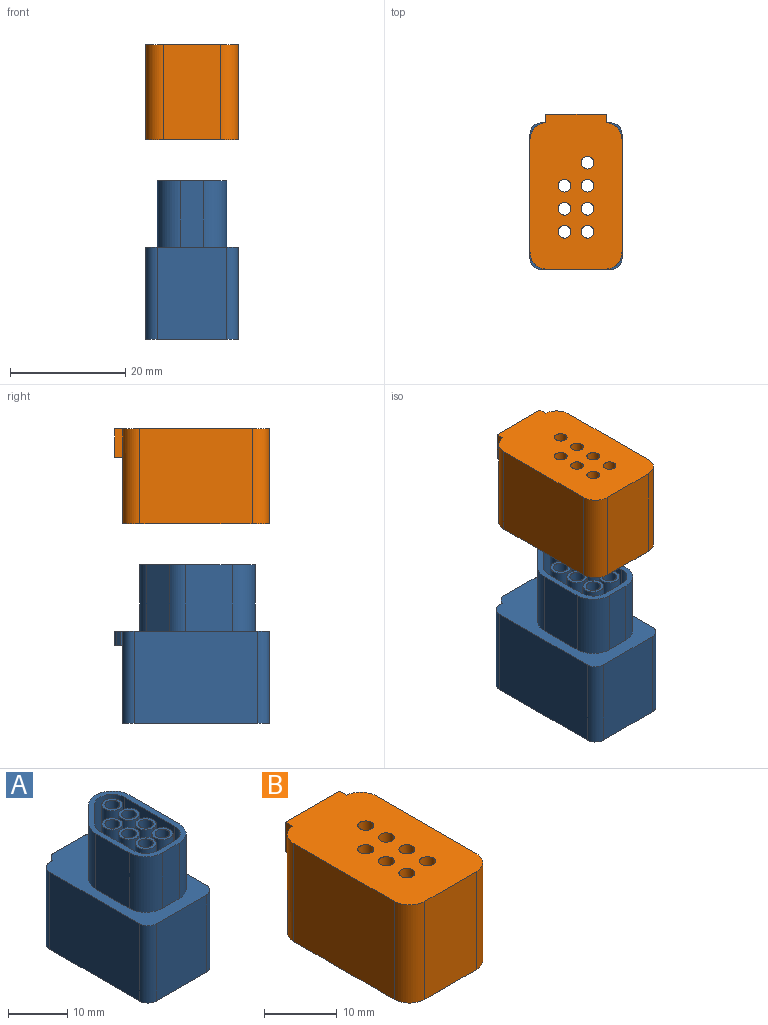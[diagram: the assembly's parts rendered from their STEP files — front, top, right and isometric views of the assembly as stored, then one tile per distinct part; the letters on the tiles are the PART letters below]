
ASSEMBLY  parts=2 mates=1
PART A: 66 faces, bbox 16x26.9x27.5 mm
  f0: cylinder r=1.25mm len=14.7mm, axis (0,0,1), area 115.5mm2, adj f17,f65
  f1: cylinder r=1.25mm len=14.7mm, axis (0,0,1), area 115.5mm2, adj f19,f65
  f2: cylinder r=1.25mm len=14.7mm, axis (0,0,1), area 115.5mm2, adj f21,f65
  f3: cylinder r=1.25mm len=14.7mm, axis (0,0,1), area 115.5mm2, adj f23,f65
  f4: cylinder r=1.25mm len=14.7mm, axis (0,0,1), area 115.5mm2, adj f25,f65
  f5: cylinder r=1.25mm len=14.7mm, axis (0,0,1), area 115.5mm2, adj f27,f65
  f6: cylinder r=1.25mm len=14.7mm, axis (0,0,1), area 115.5mm2, adj f15,f65
  f7: plane 18x10mm, normal (0,0,1), area 86mm2, adj f14,f16,f18,f20,f22,f24,f26,f35
  f8: plane 16x12mm, normal (0,1,0), area 165.7mm2, adj f12,f13,f45,f48,f49,f51,f52
  f9: plane 21.5x16mm, normal (-1,0,0), area 344mm2, adj f12,f13,f45,f46
  f10: plane 16x12mm, normal (0,-1,0), area 192mm2, adj f12,f13,f46,f47
  f11: plane 21.5x16mm, normal (1,0,0), area 344mm2, adj f12,f13,f47,f48
  f12: plane 25.5x16mm, normal (0,0,-1), area 150mm2, adj f8,f9,f10,f11,f45,f46,f47,f48
  f13: plane 26.9x16mm, normal (0,0,1), area 209.3mm2, adj f8,f9,f10,f11,f28,f29,f30,f31
  f14: cylinder r=1.8mm len=11.5mm, axis (0,0,-1), area 130.1mm2, adj f7,f15
  f15: plane 3.6x3.6mm, normal (0,0,1), area 5.3mm2, adj f6,f14
  f16: cylinder r=1.8mm len=11.5mm, axis (0,0,-1), area 130.1mm2, adj f7,f17
  f17: plane 3.6x3.6mm, normal (0,0,1), area 5.3mm2, adj f0,f16
  f18: cylinder r=1.8mm len=11.5mm, axis (0,0,-1), area 130.1mm2, adj f7,f19
  f19: plane 3.6x3.6mm, normal (0,0,1), area 5.3mm2, adj f1,f18
  f20: cylinder r=1.8mm len=11.5mm, axis (0,0,-1), area 130.1mm2, adj f7,f21
  f21: plane 3.6x3.6mm, normal (0,0,1), area 5.3mm2, adj f2,f20
  f22: cylinder r=1.8mm len=11.5mm, axis (0,0,-1), area 130.1mm2, adj f7,f23
  f23: plane 3.6x3.6mm, normal (0,0,1), area 5.3mm2, adj f3,f22
  f24: cylinder r=1.8mm len=11.5mm, axis (0,0,-1), area 130.1mm2, adj f7,f25
  f25: plane 3.6x3.6mm, normal (0,0,1), area 5.3mm2, adj f4,f24
  f26: cylinder r=1.8mm len=11.5mm, axis (0,0,-1), area 130.1mm2, adj f7,f27
  f27: plane 3.6x3.6mm, normal (0,0,1), area 5.3mm2, adj f5,f26
  f28: cylinder r=4mm len=11.5mm, axis (0,0,-1), area 72.3mm2, adj f13,f29,f43,f44
  f29: plane 11.5x4mm, normal (0,-1,0), area 46mm2, adj f13,f28,f30,f44
  f30: cylinder r=4mm len=11.5mm, axis (0,0,-1), area 72.3mm2, adj f13,f29,f31,f44
  f31: plane 12x11.5mm, normal (1,0,0), area 138mm2, adj f13,f30,f32,f44
  f32: cylinder r=4mm len=11.5mm, axis (0,0,-1), area 108.4mm2, adj f13,f31,f33,f44
  f33: plane 11.5x4mm, normal (-0.71,0.71,0), area 65.1mm2, adj f13,f32,f34,f44
  f34: cylinder r=4mm len=11.5mm, axis (0,0,-1), area 36.1mm2, adj f13,f33,f43,f44
  f35: cylinder r=3mm len=11.5mm, axis (0,0,-1), area 81.3mm2, adj f7,f36,f42,f44
  f36: plane 12x11.5mm, normal (-1,0,0), area 138mm2, adj f7,f35,f37,f44
  f37: cylinder r=3mm len=11.5mm, axis (0,0,-1), area 54.2mm2, adj f7,f36,f38,f44
  f38: plane 11.5x4mm, normal (0,1,0), area 46mm2, adj f7,f37,f39,f44
  f39: cylinder r=3mm len=11.5mm, axis (0,0,-1), area 54.2mm2, adj f7,f38,f40,f44
  f40: plane 11.5x8mm, normal (1,0,0), area 92mm2, adj f7,f39,f41,f44
  f41: cylinder r=3mm len=11.5mm, axis (0,0,-1), area 27.1mm2, adj f7,f40,f42,f44
  f42: plane 11.5x4mm, normal (0.71,-0.71,0), area 65.1mm2, adj f7,f35,f41,f44
  f43: plane 11.5x8mm, normal (-1,0,0), area 92mm2, adj f13,f28,f34,f44
  f44: plane 20x12mm, normal (0,0,1), area 51.6mm2, adj f28,f29,f30,f31,f32,f33,f34,f35
  f45: cylinder r=2mm len=16mm, axis (0,0,-1), area 50.3mm2, adj f8,f9,f12,f13
  f46: cylinder r=2mm len=16mm, axis (0,0,1), area 50.3mm2, adj f9,f10,f12,f13
  f47: cylinder r=2mm len=16mm, axis (0,0,-1), area 50.3mm2, adj f10,f11,f12,f13
  f48: cylinder r=2mm len=16mm, axis (0,0,1), area 50.3mm2, adj f8,f11,f12,f13
  f49: plane 2.5x0.4mm, normal (1,0,0), area 1mm2, adj f8,f13,f52,f54
  f50: plane 7.67x2.5mm, normal (0,1,0), area 19.2mm2, adj f13,f52,f55,f56
  f51: plane 2.5x0.4mm, normal (-1,0,0), area 1mm2, adj f8,f13,f52,f53
  f52: plane 10.5x1.4mm, normal (0,0,-1), area 13.7mm2, adj f8,f49,f50,f51,f53,f54,f55,f56
  f53: plane 2.5x0.71mm, normal (-0.71,0.71,0), area 2.5mm2, adj f13,f51,f52,f55
  f54: plane 2.5x0.71mm, normal (0.71,0.71,0), area 2.5mm2, adj f13,f49,f52,f56
  f55: cylinder r=1mm len=2.5mm, axis (0,0,1), area 2mm2, adj f13,f50,f52,f53
  f56: cylinder r=1mm len=2.5mm, axis (0,0,1), area 2mm2, adj f13,f50,f52,f54
  f57: plane 17.5x12.8mm, normal (1,0,0), area 224mm2, adj f12,f58,f64,f65
  f58: cylinder r=2mm len=12.8mm, axis (0,0,-1), area 40.2mm2, adj f12,f57,f59,f65
  f59: plane 12.8x8mm, normal (0,-1,0), area 102.4mm2, adj f12,f58,f60,f65
  f60: cylinder r=2mm len=12.8mm, axis (0,0,-1), area 40.2mm2, adj f12,f59,f61,f65
  f61: plane 17.5x12.8mm, normal (-1,0,0), area 224mm2, adj f12,f60,f62,f65
  f62: cylinder r=2mm len=12.8mm, axis (0,0,-1), area 40.2mm2, adj f12,f61,f63,f65
  f63: plane 12.8x8mm, normal (0,1,0), area 102.4mm2, adj f12,f62,f64,f65
  f64: cylinder r=2mm len=12.8mm, axis (0,0,-1), area 40.2mm2, adj f12,f57,f63,f65
  f65: plane 21.5x12mm, normal (0,0,-1), area 220.2mm2, adj f0,f1,f2,f3,f4,f5,f6,f57
PART B: 80 faces, bbox 20.1x29.4x17 mm
  f0: plane 6x4mm, normal (0,0,-1), area 4.7mm2, adj f17,f18,f51,f77
  f1: plane 6x4mm, normal (0,0,-1), area 4.7mm2, adj f18,f19,f52,f78
  f2: plane 2.16x0.65mm, normal (0,0,-1), area 0.6mm2, adj f35,f66,f67
  f3: plane 2.16x0.65mm, normal (0,0,-1), area 0.6mm2, adj f35,f62,f66
  f4: plane 2.84x2.84mm, normal (0,0,-1), area 2.6mm2, adj f41,f65,f67
  f5: plane 2.16x0.65mm, normal (0,0,-1), area 0.6mm2, adj f39,f64,f65
  f6: plane 2.16x0.65mm, normal (0,0,-1), area 0.6mm2, adj f39,f63,f64
  f7: plane 2.16x0.65mm, normal (0,0,-1), area 0.6mm2, adj f37,f61,f62
  f8: cylinder r=1.9mm len=10.5mm, axis (0,0,-1), area 125.3mm2, adj f49,f67
  f9: cylinder r=1.9mm len=10.5mm, axis (0,0,-1), area 125.3mm2, adj f48,f66
  f10: cylinder r=1.9mm len=10.5mm, axis (0,0,-1), area 125.3mm2, adj f47,f62
  f11: cylinder r=1.9mm len=10.5mm, axis (0,0,-1), area 125.3mm2, adj f46,f65
  f12: cylinder r=1.9mm len=10.5mm, axis (0,0,-1), area 125.3mm2, adj f45,f64
  f13: cylinder r=1.9mm len=10.5mm, axis (0,0,-1), area 125.3mm2, adj f44,f63
  f14: cylinder r=1.9mm len=10.5mm, axis (0,0,-1), area 125.3mm2, adj f43,f61
  f15: plane 21x13mm, normal (0,0,-1), area 91.8mm2, adj f25,f26,f27,f28,f29,f30,f31,f32
  f16: plane 5x1.41mm, normal (-1,0,0), area 7.1mm2, adj f22,f23,f24,f50
  f17: plane 19.55x16.55mm, normal (-1,0,0), area 321.8mm2, adj f0,f23,f33,f50,f51,f71,f73,f75
  f18: plane 16.5x10mm, normal (0,-1,0), area 165mm2, adj f0,f1,f23,f51,f52,f79
  f19: plane 19.55x16.55mm, normal (1,0,0), area 321.8mm2, adj f1,f23,f33,f52,f53,f72,f74,f76
  f20: plane 11.5x10mm, normal (0,1,0), area 115mm2, adj f24,f33,f50,f53
  f21: plane 5x1.41mm, normal (1,0,0), area 7.1mm2, adj f22,f23,f24,f53
  f22: plane 10.5x5mm, normal (0,1,0), area 52.5mm2, adj f16,f21,f23,f24
  f23: plane 26.9x16mm, normal (0,0,1), area 388.4mm2, adj f16,f17,f18,f19,f21,f22,f50,f51
  f24: plane 10.5x1.41mm, normal (0,0,-1), area 14.7mm2, adj f16,f20,f21,f22,f50,f53
  f25: plane 9.56x8mm, normal (1,0,0), area 76.5mm2, adj f15,f26,f32,f73
  f26: cylinder r=4.5mm len=9.56mm, axis (0,0,1), area 33.6mm2, adj f15,f25,f27,f69,f71
  f27: plane 9.5x4mm, normal (0.71,-0.71,0), area 53.7mm2, adj f15,f26,f28,f68
  f28: cylinder r=4.5mm len=9.56mm, axis (0,0,1), area 100.8mm2, adj f15,f27,f29,f70,f72
  f29: plane 12x9.56mm, normal (-1,0,0), area 114.8mm2, adj f15,f28,f30,f74
  f30: cylinder r=4.5mm len=9.56mm, axis (0,0,1), area 67.2mm2, adj f15,f29,f31,f76,f78
  f31: plane 9.5x4mm, normal (0,1,0), area 38mm2, adj f15,f30,f32,f79
  f32: cylinder r=4.5mm len=9.56mm, axis (0,0,1), area 67.2mm2, adj f15,f25,f31,f75,f77
  f33: plane 16x8.5mm, normal (0,0,-1), area 38.7mm2, adj f17,f19,f20,f50,f53,f68,f69,f70
  f34: cylinder r=2.75mm len=11.49mm, axis (0,0,1), area 24.8mm2, adj f15,f35,f41,f67
  f35: plane 11.8x8.3mm, normal (-1,0,0), area 92mm2, adj f2,f3,f15,f34,f36,f62,f66,f67
  f36: cylinder r=2.75mm len=11.49mm, axis (0,0,1), area 49.6mm2, adj f15,f35,f37,f62
  f37: plane 11.58x4.08mm, normal (0,-1,0), area 46mm2, adj f7,f15,f36,f38,f61,f62
  f38: cylinder r=2.75mm len=11.49mm, axis (0,0,1), area 49.6mm2, adj f15,f37,f39,f61
  f39: plane 12.08x11.58mm, normal (1,0,0), area 138mm2, adj f5,f6,f15,f38,f40,f42,f61,f63
  f40: cylinder r=2.75mm len=11.49mm, axis (0,0,1), area 74.4mm2, adj f15,f39,f41,f65
  f41: plane 11.58x4.08mm, normal (-0.71,0.71,0), area 65mm2, adj f4,f15,f34,f40,f65,f67
  f42: plane 2.16x0.65mm, normal (0,0,-1), area 0.6mm2, adj f39,f61,f63
  f43: plane 3.8x3.8mm, normal (0,0,-1), area 7.5mm2, adj f14,f54
  f44: plane 3.8x3.8mm, normal (0,0,-1), area 7.5mm2, adj f13,f57
  f45: plane 3.8x3.8mm, normal (0,0,-1), area 7.5mm2, adj f12,f59
  f46: plane 3.8x3.8mm, normal (0,0,-1), area 7.5mm2, adj f11,f60
  f47: plane 3.8x3.8mm, normal (0,0,-1), area 7.5mm2, adj f10,f55
  f48: plane 3.8x3.8mm, normal (0,0,-1), area 7.5mm2, adj f9,f56
  f49: plane 3.8x3.8mm, normal (0,0,-1), area 7.5mm2, adj f8,f58
  f50: cylinder r=3mm len=16.5mm, axis (0,0,1), area 76.5mm2, adj f16,f17,f20,f23,f24,f33
  f51: cylinder r=3mm len=16.5mm, axis (0,0,-1), area 77.8mm2, adj f0,f17,f18,f23
  f52: cylinder r=3mm len=16.5mm, axis (0,0,1), area 77.8mm2, adj f1,f18,f19,f23
  f53: cylinder r=3mm len=16.5mm, axis (0,0,-1), area 76.5mm2, adj f19,f20,f21,f23,f24,f33
  f54: cylinder r=1.1mm len=5mm, axis (0,0,-1), area 34.6mm2, adj f23,f43
  f55: cylinder r=1.1mm len=5mm, axis (0,0,-1), area 34.6mm2, adj f23,f47
  f56: cylinder r=1.1mm len=5mm, axis (0,0,-1), area 34.6mm2, adj f23,f48
  f57: cylinder r=1.1mm len=5mm, axis (0,0,-1), area 34.6mm2, adj f23,f44
  f58: cylinder r=1.1mm len=5mm, axis (0,0,-1), area 34.6mm2, adj f23,f49
  f59: cylinder r=1.1mm len=5mm, axis (0,0,-1), area 34.6mm2, adj f23,f45
  f60: cylinder r=1.1mm len=5mm, axis (0,0,-1), area 34.6mm2, adj f23,f46
  f61: torus R=2.9mm, axis (0,0,1), area 16.2mm2, adj f7,f14,f37,f38,f39,f42,f62,f63
  f62: torus R=2.9mm, axis (0,0,1), area 16.2mm2, adj f3,f7,f10,f35,f36,f37,f61,f66
  f63: torus R=2.9mm, axis (0,0,1), area 13.9mm2, adj f6,f13,f39,f42,f61,f64,f66
  f64: torus R=2.9mm, axis (0,0,1), area 13.9mm2, adj f5,f6,f12,f39,f63,f65,f67
  f65: torus R=2.9mm, axis (0,0,1), area 18.2mm2, adj f4,f5,f11,f39,f40,f41,f64,f67
  f66: torus R=2.9mm, axis (0,0,1), area 14mm2, adj f2,f3,f9,f35,f62,f63,f67
  f67: torus R=2.9mm, axis (0,0,1), area 16.5mm2, adj f2,f4,f8,f34,f35,f41,f64,f65
  f68: cylinder r=2mm len=5.41mm, axis (-0.71,-0.71,0), area 17.8mm2, adj f27,f33,f69,f70
  f69: torus R=6.5mm, axis (0,0,1), area 6.4mm2, adj f26,f33,f68,f71
  f70: torus R=6.5mm, axis (0,0,1), area 32.2mm2, adj f28,f33,f68,f72
  f71: bspline ~3.3x2.25mm, area 5.6mm2, adj f17,f26,f69,f73
  f72: bspline ~3.3x2.25mm, area 5.6mm2, adj f19,f28,f70,f74
  f73: cylinder r=2mm len=8mm, axis (0,-1,0), area 21.1mm2, adj f17,f25,f71,f75
  f74: cylinder r=2mm len=12mm, axis (0,-1,0), area 31.6mm2, adj f19,f29,f72,f76
  f75: bspline ~3.3x2.25mm, area 5.6mm2, adj f17,f32,f73,f77
  f76: bspline ~3.3x2.25mm, area 5.6mm2, adj f19,f30,f74,f78
  f77: torus R=6.5mm, axis (0,0,1), area 19.3mm2, adj f0,f32,f75,f79
  f78: torus R=6.5mm, axis (0,0,1), area 19.3mm2, adj f1,f30,f76,f79
  f79: cylinder r=2mm len=4mm, axis (1,0,0), area 12.6mm2, adj f18,f31,f77,f78
PLACE A t=(2.7,-12.17,-6.79)mm
PLACE B t=(2.7,-12.17,23.35)mm
MATE slider A.f2 <-> B.f11  axis (0,0,1) through (4.7,-6.42,4.71)mm
